# Revit family: ASH_ArmitageShanks_WCSeats_Contour21_Splash305SeatAndCover
name_source: partatom
category: Plumbing Fixtures
revit_build: Autodesk Revit MEP 2012 (Build: 20110309_2315(x64)
units: mm (PartAtom-declared; Revit-internal decimal feet)

## types (4) — shared parameters
Accessories = www.idealspec.co.uk
AreaUnits = millimeters
Assembly Code = C1030200
AssetType = Fixed
BIMObjectName = ASH_ArmitageShanks_WCSeats_Contour21Splash_S4533
Brand = Armitage Shanks
ConnectionType = Mechanical
Default Elevation = 1219 mm
Description = Contour 21 splash seat and cover for 305 mm bowls
DurationUnit = year
ECA = No
ExpectedLife = 15
Features = Seat and cover for 305 mm bowls
Help = www.idealspec.co.uk/contact-us.html
IfcExportAs = IfcSanitaryTerminalType
IfcExportType = WCSEAT
InstallationInstructions = www.idealspec.co.uk/resources.html
LinearUnits = millimeters
ManufacturerURL = www.idealspec.co.uk
Material = Plastic
ModelReference = Contour 21 splash seat and cover for 305 mm bowls
NBSDescription = WC seats and covers
NBSReference = 45-35-70/391
Name = WCSeats_Contour21Splash-S4533_ArmitageShanks
NettWeight = 2.7 kg
NominalDepth = 398 mm
NominalLength = 398 mm
NominalWidth = 400 mm  [stored 1.31234 ft]
SeatColor = White
SeatHasCover = Yes
SeatMaterial = Plastic
SeatType = RingSeat
Shape = Sculptured
Space = Internal
SpareParts = www.fastpart-spares.co.uk
URL = www.idealspec.co.uk
Uniclass2 = Pr_40_20_93_95
Version = 2
VolumeUnits = Litres
WRAS = No
WarrantyDescription = Manufacturers Warranty
WarrantyDurationParts = 5
WarrantyDurationUnit = year
WaterEfficientProduct = No
zero-valued in all types: CWFU, Cost, HWFU, WFU

## per-type parameters (varying)
| type | Color | Finish | Model | ModelNumber | NominalHeight | ProductInformation | SeatSKU | Size |
| S453301-Contour 21 Splash seat and cover for 305mm bowls -White | White | White | S453301 | S453301 | 0 mm  [stored 0 ft] | www.idealspec.co.uk/assets/datasheet/S453301 | ASH_ArmitageShanks _WC_White1_Render | x x mm |
| S453379-Contour 21 Splash seat and cover for 305mm bowls - Yellow | Yellow | Yellow | S453379 | S453379 | 0 mm  [stored 0 ft] | www.idealspec.co.uk/assets/datasheet/S453379 | ASH_ArmitageShanks _WCSeat_Yellow_Render | x x mm |
| S453336-Contour 21 Splash seat and cover for 305mm bowls - Blue | Blue | Blue | S453336 | S453336 | 0 mm  [stored 0 ft] | www.idealspec.co.uk/assets/datasheet/S453336 | ASH_ArmitageShanks _WC_Blue_Render | x x mm |
| S4533GQ-Contour 21 Splash seat and cover for 305mm bowls - Red | Red | Red | S4533GQ | S4533GQ | 75 mm | www.idealspec.co.uk/assets/datasheet/S4533GQ | ASH_ArmitageShanks _WC_Red_Render | 400 x 400 x 75 mm |

note: [stored X ft] marks values corroborated as IEEE doubles in the binary element streams (Revit-internal decimal feet)
